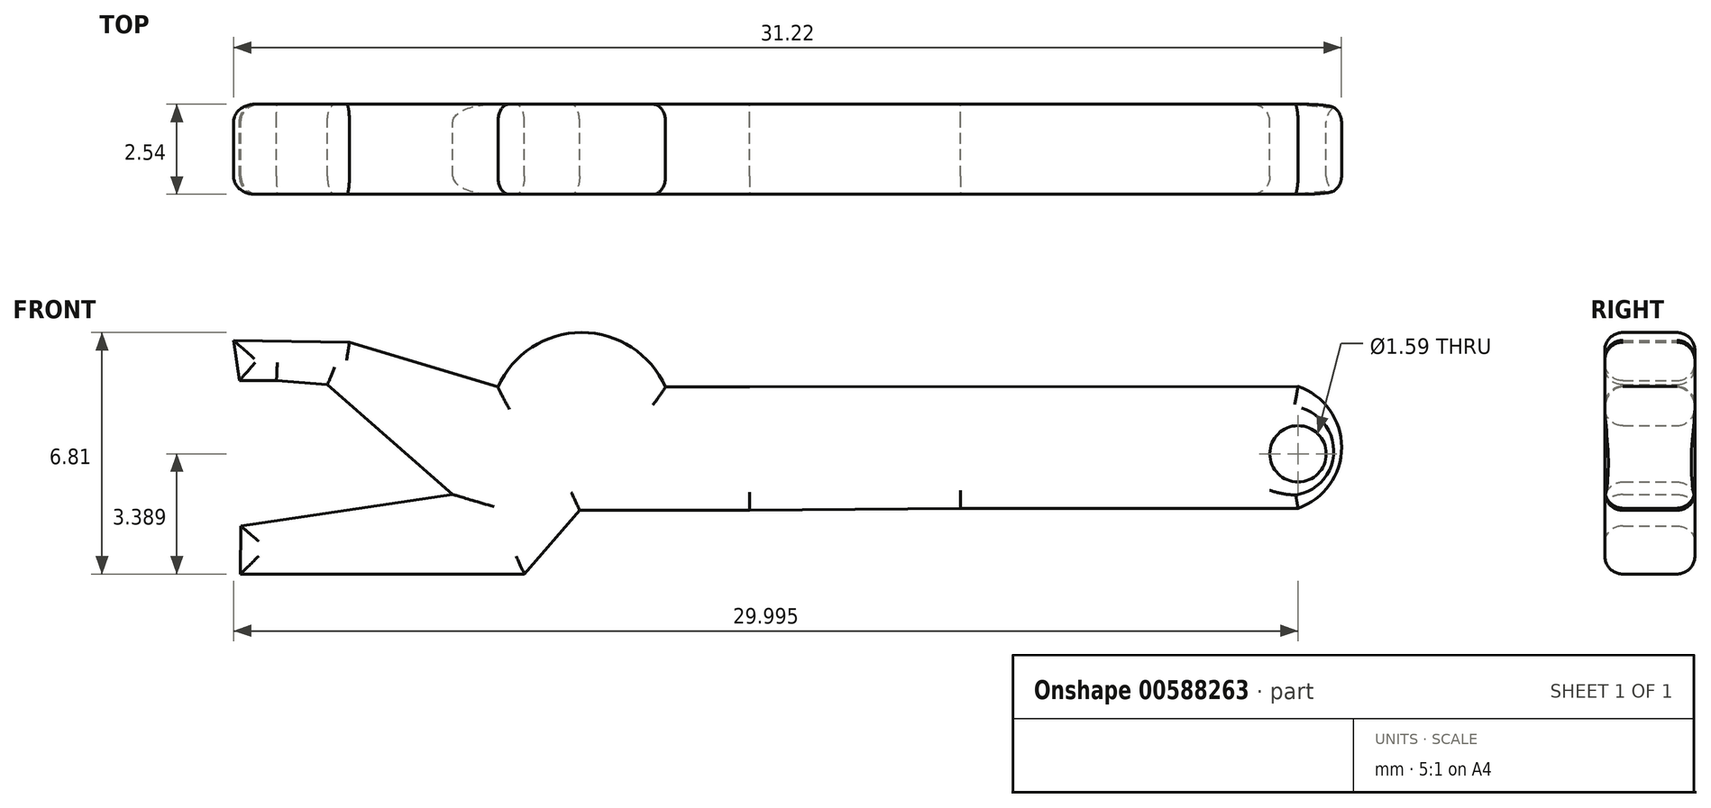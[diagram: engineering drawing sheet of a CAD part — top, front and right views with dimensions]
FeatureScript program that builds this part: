
annotation { "Feature Type Name" : "Feature", "Feature Type Description" : "" }
export const myFeature = defineFeature(function(context is Context, id is Id, definition is map)
    precondition{}
    {
        {
            var Q0;
            Q0=qCreatedBy(makeId("Front.planeOp"),FACE);
            var sketch = newSketch(context, id + "F0", { "sketchPlane" : qUnion([Q0])});
            skLineSegment(sketch, "E0", {"start": v(-47.33, 21.88) * mm, "end": v(-48.89, 20.09) * mm});
            skLineSegment(sketch, "E1", {"start": v(-48.89, 20.09) * mm, "end": v(-56.89, 20.09) * mm});
            skLineSegment(sketch, "E2", {"start": v(-36.6, 21.94) * mm, "end": v(-29.28, 21.94) * mm});
            skLineSegment(sketch, "E3", {"start": v(-42.54, 21.88) * mm, "end": v(-36.6, 21.94) * mm});
            skPoint(sketch, "E4", {"position": v(-27.08, 23.48) * mm});
            skArc(sketch, "E5", {"start": v(-27.08, 21.94) * mm, "mid": v(-25.86, 23.67) * mm, "end": v(-27.08, 25.39) * mm});
            skLineSegment(sketch, "E6", {"start": v(-27.08, 25.39) * mm, "end": v(-42.54, 25.36) * mm});
            skLineSegment(sketch, "E7", {"start": v(-29.28, 21.94) * mm, "end": v(-27.08, 21.94) * mm});
            skArc(sketch, "E8", {"start": v(-44.91, 25.36) * mm, "mid": v(-47.27, 26.9) * mm, "end": v(-49.63, 25.36) * mm});
            skLineSegment(sketch, "E9", {"start": v(-47.33, 21.88) * mm, "end": v(-42.54, 21.88) * mm});
            skLineSegment(sketch, "E10", {"start": v(-49.63, 25.36) * mm, "end": v(-53.82, 26.63) * mm});
            skLineSegment(sketch, "E11", {"start": v(-42.54, 25.36) * mm, "end": v(-44.91, 25.36) * mm});
            skLineSegment(sketch, "E12", {"start": v(-56.88, 21.45) * mm, "end": v(-56.89, 20.09) * mm});
            skPoint(sketch, "E13.endSnap0", {"position": v(-44.93, 23.19) * mm});
            skLineSegment(sketch, "E14", {"start": v(-50.9, 22.33) * mm, "end": v(-54.44, 25.43) * mm});
            skLineSegment(sketch, "E15", {"start": v(-54.44, 25.43) * mm, "end": v(-55.87, 25.54) * mm});
            skLineSegment(sketch, "E16", {"start": v(-55.87, 25.54) * mm, "end": v(-56.92, 25.54) * mm});
            skLineSegment(sketch, "E17", {"start": v(-56.92, 25.54) * mm, "end": v(-57.08, 26.68) * mm});
            skLineSegment(sketch, "E18", {"start": v(-57.08, 26.68) * mm, "end": v(-53.82, 26.63) * mm});
            skLineSegment(sketch, "E19", {"start": v(-56.88, 21.45) * mm, "end": v(-50.9, 22.33) * mm});
            skSolve(sketch);
        }
        {
            var Q0;
            {var subQ2=sQuery(id+"F0.wireOp",EDGE,"E0");Q0=makeQuery(id+"F0.imprint","IMPRINT",FACE,{"disambiguationData":[TD([[makeQuery(id+"F0.imprint","IMPRINT",EDGE,{"derivedFrom":subQ2}),-1.0]])]});}
            var Q1;
            {var subQ0=sQuery(id+"F0.wireOp",EDGE,"IC0lPeA7-vqVf-iQRE-a2C1-sJKCqJrvt4kN");Q1=makeQuery(id+"F0.imprint","IMPRINT",FACE,{"disambiguationData":[TD([[makeQuery(id+"F0.imprint","IMPRINT",EDGE,{"derivedFrom":subQ0}),-1.0]])]});}
            var Q2;
            {var subQ0=sQuery(id+"F0.wireOp",EDGE,"VuNUg2Xb-UkDo-7Hs7-5yw9-32M97kZEPfqA");Q2=makeQuery(id+"F0.imprint","IMPRINT",FACE,{"disambiguationData":[TD([[makeQuery(id+"F0.imprint","IMPRINT",EDGE,{"derivedFrom":subQ0}),1.0]])]});}
            var Q3;
            {var subQ0=sQuery(id+"F0.wireOp",EDGE,"ksxhWLGx-EDF9-xJSU-qI5r-BT0spQioLxzj");Q3=makeQuery(id+"F0.imprint","IMPRINT",FACE,{"disambiguationData":[TD([[makeQuery(id+"F0.imprint","IMPRINT",EDGE,{"derivedFrom":subQ0}),1.0]])]});}
            var Q4;
            {var subQ0=sQuery(id+"F0.wireOp",EDGE,"qSTFRSEV-d1Y7-B9Xn-jkGr-stS26H4VY3pj");Q4=makeQuery(id+"F0.imprint","IMPRINT",FACE,{"disambiguationData":[TD([[makeQuery(id+"F0.imprint","IMPRINT",EDGE,{"derivedFrom":subQ0}),1.0]])]});}
            var Q5;
            {var subQ0=sQuery(id+"F0.wireOp",EDGE,"E8");Q5=makeQuery(id+"F0.imprint","IMPRINT",FACE,{"disambiguationData":[TD([[makeQuery(id+"F0.imprint","IMPRINT",EDGE,{"derivedFrom":subQ0}),1.0]])]});}
            var Q6;
            Q6=makeQuery(id+"F0.imprint","IMPRINT",FACE,{"disambiguationData":[TD([[makeQuery(id+"F0.imprint","IMPRINT",EDGE,{"derivedFrom":sQuery(id+"F0.wireOp",EDGE,"EPSZcfWV-7bKO-GKsC-rJfJ-6VYxb7qcYclh")}),1.0]])]});
            var Q7;
            {var subQ0=sQuery(id+"F0.wireOp",EDGE,"gPsp1tlT-OIQw-xfoc-ON93-4dtUerIXfKEJ");Q7=makeQuery(id+"F0.imprint","IMPRINT",FACE,{"disambiguationData":[TD([[makeQuery(id+"F0.imprint","IMPRINT",EDGE,{"derivedFrom":subQ0}),1.0]])]});}
            extrude(context, id + "F1", {"entities" : qUnion([Q0, Q1, Q2, Q3, Q4, Q5, Q6, Q7]), "depth" : 2.54 * mm, "offsetDistance" : 25.4 * mm});
        }
        {
            var Q0;
            Q0=sQuery(id+"F0.wireOp",VERTEX,"E4");
            var Q1;
            Q1=makeQuery(id+"F1.opExtrude","SWEPT_BODY",BODY,{"disambiguationData":[OSD([sQuery(id+"F0.wireOp",EDGE,"GRa3V7gF-RJev-0JcZ-ybxQ-HxstfmS0LVlb"),sQuery(id+"F0.wireOp",EDGE,"qEMiysxi-RZzI-DY4A-rcNR-qGkVmeCNaxwS"),sQuery(id+"F0.wireOp",EDGE,"QUCyJpdy-qRHU-009u-GRsp-DbGE76QC2mQr"),sQuery(id+"F0.wireOp",EDGE,"IC0lPeA7-vqVf-iQRE-a2C1-sJKCqJrvt4kN"),sQuery(id+"F0.wireOp",EDGE,"E0"),sQuery(id+"F0.wireOp",EDGE,"E1"),sQuery(id+"F0.wireOp",EDGE,"vwsqvquj-DKYB-uNFm-SnuQ-jbtAWcN9007X"),sQuery(id+"F0.wireOp",EDGE,"E2"),sQuery(id+"F0.wireOp",EDGE,"OJWDnuZs-b236-CzYF-MCnQ-ovPQr3OlZxzL"),sQuery(id+"F0.wireOp",EDGE,"EPSZcfWV-7bKO-GKsC-rJfJ-6VYxb7qcYclh"),sQuery(id+"F0.wireOp",EDGE,"E3")])]});
            hole(context, id + "F2", {"style" : HoleStyle.SIMPLE, "endStyle" : HoleEndStyle.THROUGH, "oppositeDirection" : true, "holeDiameter" : 1.59 * mm, "majorDiameter" : 6.35 * mm, "isTappedThrough" : true, "tappedDepth" : 12.7 * mm, "tapClearance" : 3, "locations" : qUnion([Q0]), "scope" : qUnion([Q1])});
        }
        {
            var Q0;
            Q0=makeQuery(id+"F1.opExtrude","CAP_FACE",FACE,{"disambiguationData":[OSD([sQuery(id+"F0.wireOp",EDGE,"E0"),sQuery(id+"F0.wireOp",EDGE,"E1"),sQuery(id+"F0.wireOp",EDGE,"E2"),sQuery(id+"F0.wireOp",EDGE,"E3"),sQuery(id+"F0.wireOp",EDGE,"E5"),sQuery(id+"F0.wireOp",EDGE,"E6"),sQuery(id+"F0.wireOp",EDGE,"E7"),sQuery(id+"F0.wireOp",EDGE,"E8"),sQuery(id+"F0.wireOp",EDGE,"E9"),sQuery(id+"F0.wireOp",EDGE,"E10"),sQuery(id+"F0.wireOp",EDGE,"E11"),sQuery(id+"F0.wireOp",EDGE,"E12"),sQuery(id+"F0.wireOp",EDGE,"E14"),sQuery(id+"F0.wireOp",EDGE,"E15"),sQuery(id+"F0.wireOp",EDGE,"E16"),sQuery(id+"F0.wireOp",EDGE,"E17"),sQuery(id+"F0.wireOp",EDGE,"E18"),sQuery(id+"F0.wireOp",EDGE,"E19")])],"isStart":false});
            var Q1;
            Q1=makeQuery(id+"F1.opExtrude","CAP_FACE",FACE,{"disambiguationData":[OSD([sQuery(id+"F0.wireOp",EDGE,"E0"),sQuery(id+"F0.wireOp",EDGE,"E1"),sQuery(id+"F0.wireOp",EDGE,"E2"),sQuery(id+"F0.wireOp",EDGE,"E3"),sQuery(id+"F0.wireOp",EDGE,"E5"),sQuery(id+"F0.wireOp",EDGE,"E6"),sQuery(id+"F0.wireOp",EDGE,"E7"),sQuery(id+"F0.wireOp",EDGE,"E8"),sQuery(id+"F0.wireOp",EDGE,"E9"),sQuery(id+"F0.wireOp",EDGE,"E10"),sQuery(id+"F0.wireOp",EDGE,"E11"),sQuery(id+"F0.wireOp",EDGE,"E12"),sQuery(id+"F0.wireOp",EDGE,"E14"),sQuery(id+"F0.wireOp",EDGE,"E15"),sQuery(id+"F0.wireOp",EDGE,"E16"),sQuery(id+"F0.wireOp",EDGE,"E17"),sQuery(id+"F0.wireOp",EDGE,"E18"),sQuery(id+"F0.wireOp",EDGE,"E19")])],"isStart":true});
            fillet(context, id + "F3", {"entities" : qUnion([Q0, Q1]), "radius" : 0.5 * mm, "tangentPropagation" : true, "allowEdgeOverflow" : false});
        }
    });
